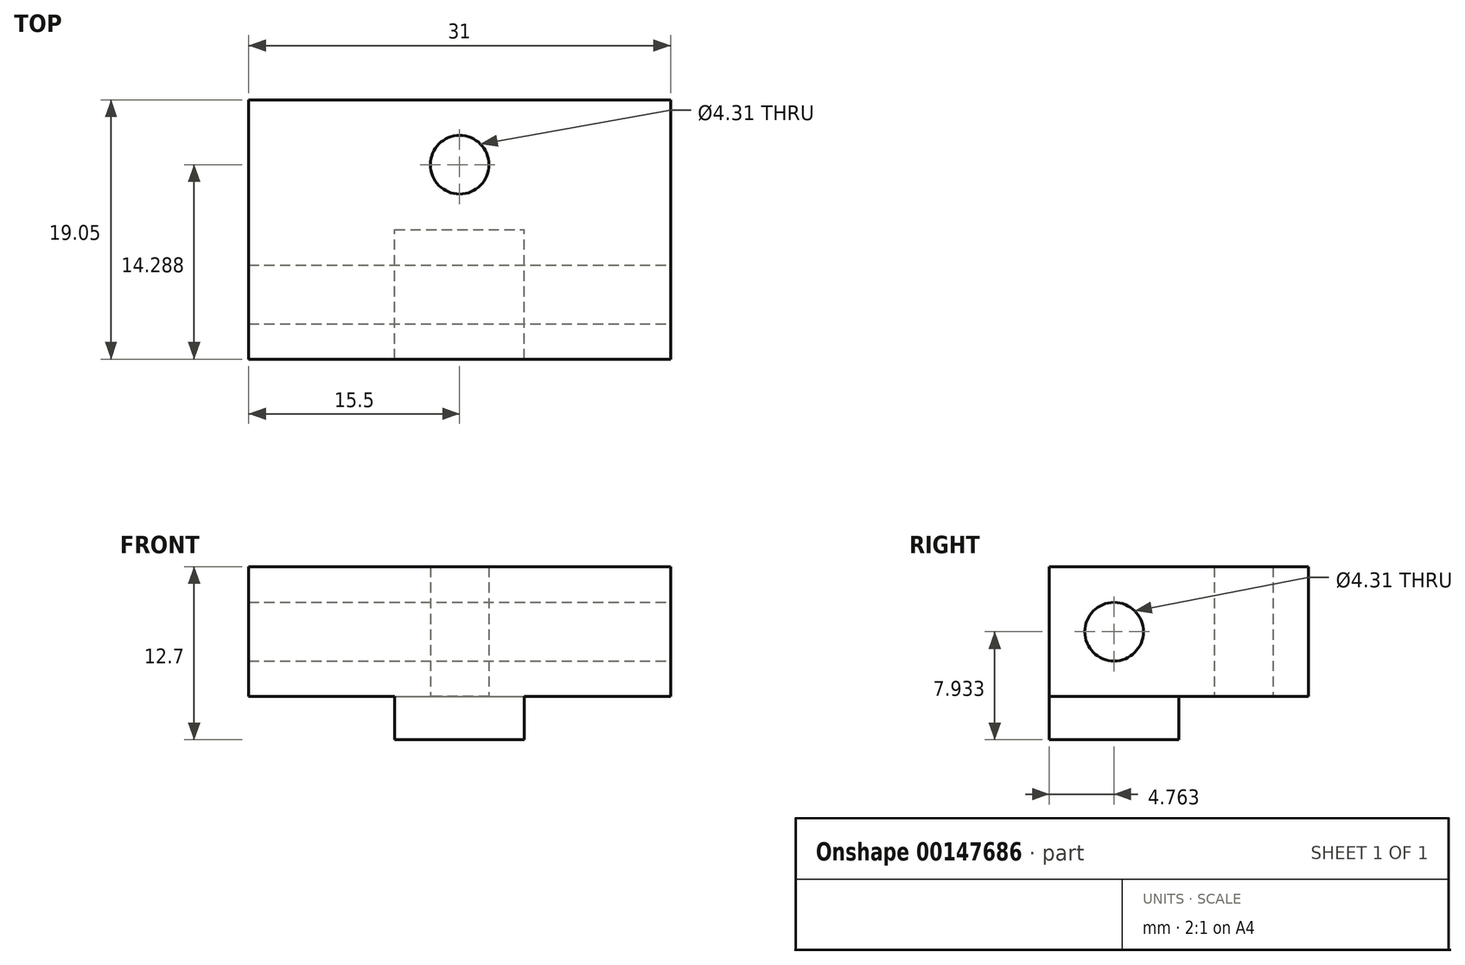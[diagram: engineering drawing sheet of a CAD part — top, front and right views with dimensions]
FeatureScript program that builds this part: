
annotation { "Feature Type Name" : "Feature", "Feature Type Description" : "" }
export const myFeature = defineFeature(function(context is Context, id is Id, definition is map)
    precondition{}
    {
        {
            var Q0;
            Q0=qCreatedBy(makeId("Top.planeOp"),FACE);
            var sketch = newSketch(context, id + "F0", { "sketchPlane" : qUnion([Q0])});
            skLineSegment(sketch, "E0.bottom", {"start": v(0, 0) * mm, "end": v(31, 0) * mm});
            skLineSegment(sketch, "E0.top", {"start": v(0, -19.05) * mm, "end": v(31, -19.05) * mm});
            skLineSegment(sketch, "E0.left", {"start": v(0, 0) * mm, "end": v(0, -19.05) * mm});
            skLineSegment(sketch, "E0.right", {"start": v(31, 0) * mm, "end": v(31, -19.05) * mm});
            skLineSegment(sketch, "E1", {"start": v(15.5, 0) * mm, "end": v(15.5, -4.76) * mm, "construction": true});
            skCircle(sketch, "E2", {"center": v(15.5, -4.76) * mm, "radius": 2.15 * mm});
            skLineSegment(sketch, "E3", {"start": v(15.5, -4.76) * mm, "end": v(0, -4.76) * mm, "construction": true});
            skSolve(sketch);
        }
        {
            var Q0;
            Q0=qSketchRegion(id+"F0",true);
            extrude(context, id + "F1", {"entities" : qUnion([Q0]), "depth" : 9.52 * mm});
        }
        {
            var Q0;
            Q0=makeQuery(id+"F1.opExtrude","SWEPT_FACE",FACE,{"disambiguationData":[OSD([sQuery(id+"F0.wireOp",EDGE,"E0.right")])]});
            var sketch = newSketch(context, id + "F2", { "sketchPlane" : qUnion([Q0])});
            skLineSegment(sketch, "E4", {"start": v(0, 4.76) * mm, "end": v(-14.29, 4.76) * mm, "construction": true});
            skCircle(sketch, "E5", {"center": v(-14.29, 4.76) * mm, "radius": 2.15 * mm});
            skSolve(sketch);
        }
        {
            var Q0;
            Q0=qSketchRegion(id+"F2",true);
            var Q1;
            Q1=makeQuery(id+"F1.opExtrude","SWEPT_FACE",FACE,{"disambiguationData":[OSD([sQuery(id+"F0.wireOp",EDGE,"E0.left")])]});
            extrude(context, id + "F3", {"entities" : qUnion([Q0]), "operationType" : NewBodyOperationType.REMOVE, "endBound" : BoundingType.UP_TO_SURFACE, "oppositeDirection" : true, "endBoundEntityFace" : qUnion([Q1]), "depth" : 25.4 * mm});
        }
        {
            var Q0;
            Q0=makeQuery(id+"F1.opExtrude","CAP_FACE",FACE,{"disambiguationData":[OSD([sQuery(id+"F0.wireOp",EDGE,"E0.bottom"),sQuery(id+"F0.wireOp",EDGE,"E0.top"),sQuery(id+"F0.wireOp",EDGE,"E0.left"),sQuery(id+"F0.wireOp",EDGE,"E0.right"),sQuery(id+"F0.wireOp",EDGE,"E2"),sQuery(id+"F0.wireOp",EDGE,"LaN50Wi6-CAFj-wKd2-t5ty-lVtg32UNv0FP")])],"isStart":true});
            var sketch = newSketch(context, id + "F4", { "sketchPlane" : qUnion([Q0])});
            skLineSegment(sketch, "E6.bottom", {"start": v(10.74, 19.05) * mm, "end": v(20.26, 19.05) * mm});
            skLineSegment(sketch, "E6.top", {"start": v(10.74, 9.52) * mm, "end": v(20.26, 9.52) * mm});
            skLineSegment(sketch, "E6.left", {"start": v(10.74, 19.05) * mm, "end": v(10.74, 9.52) * mm});
            skLineSegment(sketch, "E6.right", {"start": v(20.26, 19.05) * mm, "end": v(20.26, 9.52) * mm});
            skPoint(sketch, "E7", {"position": v(15.5, 19.05) * mm});
            skSolve(sketch);
        }
        {
            var Q0;
            Q0=qSketchRegion(id+"F4",true);
            extrude(context, id + "F5", {"entities" : qUnion([Q0]), "operationType" : NewBodyOperationType.ADD, "depth" : 3.17 * mm});
        }
    });
